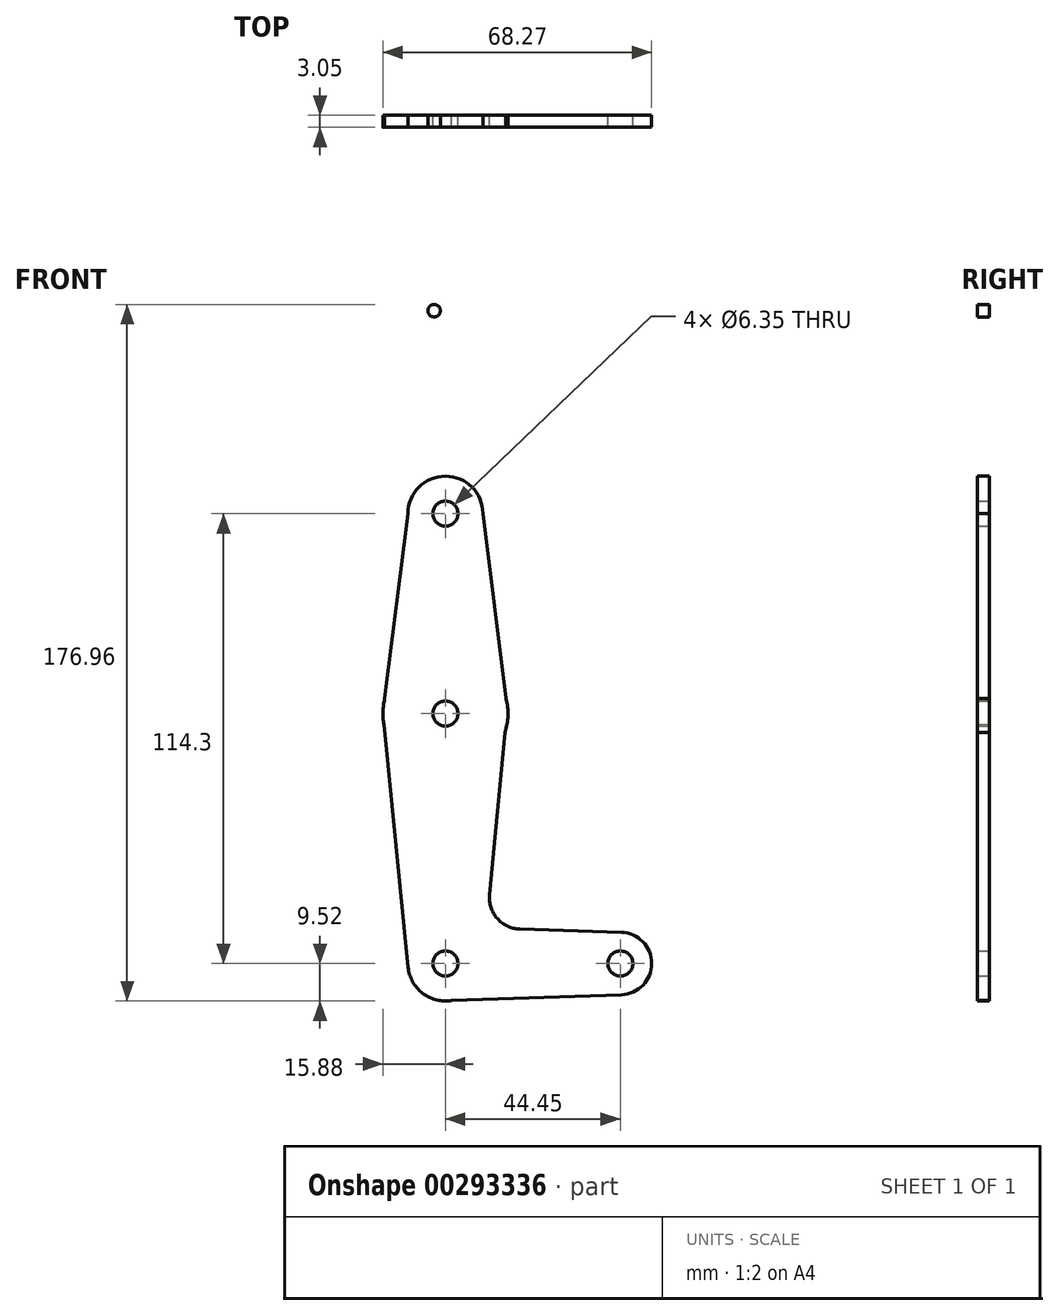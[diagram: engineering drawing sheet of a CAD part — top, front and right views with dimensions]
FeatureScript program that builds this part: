
annotation { "Feature Type Name" : "Feature", "Feature Type Description" : "" }
export const myFeature = defineFeature(function(context is Context, id is Id, definition is map)
    precondition{}
    {
        {
            var Q0;
            Q0=qCreatedBy(makeId("Front.planeOp"),FACE);
            var sketch = newSketch(context, id + "F0", { "sketchPlane" : qUnion([Q0])});
            skCircle(sketch, "E0", {"center": v(0, 0) * mm, "radius": 9.53 * mm});
            skCircle(sketch, "E1", {"center": v(0, 63.5) * mm, "radius": 15.88 * mm});
            skCircle(sketch, "E2", {"center": v(0, 114.3) * mm, "radius": 9.53 * mm});
            skCircle(sketch, "E3", {"center": v(44.45, 0) * mm, "radius": 7.94 * mm});
            skLineSegment(sketch, "E4", {"start": v(0, 0) * mm, "end": v(0, 63.5) * mm, "construction": true});
            skLineSegment(sketch, "E5", {"start": v(0, 63.5) * mm, "end": v(0, 114.3) * mm, "construction": true});
            skLineSegment(sketch, "E6", {"start": v(0, 0) * mm, "end": v(44.45, 0) * mm, "construction": true});
            skLineSegment(sketch, "E7", {"start": v(15.42, 67.27) * mm, "end": v(9.52, 114.3) * mm});
            skLineSegment(sketch, "E8", {"start": v(-15.42, 67.27) * mm, "end": v(-9.52, 114.3) * mm});
            skCircle(sketch, "E9", {"center": v(0, 114.3) * mm, "radius": 3.18 * mm});
            skCircle(sketch, "E10", {"center": v(-2.87, 165.85) * mm, "radius": 1.59 * mm});
            skCircle(sketch, "E11", {"center": v(0, 63.5) * mm, "radius": 3.18 * mm});
            skCircle(sketch, "E12", {"center": v(0, 0) * mm, "radius": 3.18 * mm});
            skCircle(sketch, "E13", {"center": v(44.45, 0) * mm, "radius": 3.18 * mm});
            skLineSegment(sketch, "E14", {"start": v(-15.63, 60.73) * mm, "end": v(-9.48, -0.95) * mm});
            skLineSegment(sketch, "E15", {"start": v(15.13, 58.7) * mm, "end": v(11.22, 17.45) * mm});
            skLineSegment(sketch, "E16", {"start": v(18.88, 8.75) * mm, "end": v(44.7, 7.93) * mm});
            skLineSegment(sketch, "E17", {"start": v(1.6, -9.39) * mm, "end": v(44.72, -7.93) * mm});
            skArc(sketch, "E18.filletArc", {"start": v(11.22, 17.45) * mm, "mid": v(13.17, 11.44) * mm, "end": v(18.88, 8.75) * mm});
            skSolve(sketch);
        }
        {
            var Q0;
            Q0 = qSketchRegion(id + "F0", true);
            extrude(context, id + "F1", {"entities" : qUnion([Q0]), "depth" : 3.05 * mm});
        }
    });
